# Revit family: КПД_Eng
name_source: partatom
category: Duct Accessories
units: mm (PartAtom-declared; Revit-internal decimal feet)

## family parameters
Always vertical = Yes
Cut with Voids When Loaded = No
Part Type = Attaches To
Round Connector Dimension = Use Diameter
Shared = No
Work Plane-Based = No

## types (184) — shared parameters
00_20_Manufacturer = Vents
00_20_Name = Multi-purpose fire safety smoke damper
Frequency = 50 Hz
Load Classification = HVAC
Maintenance zone material = <By Category>
Manufacturer = Vents
Maximum Air Flow = 0.0 L/s
Number of Fase = 1
URL = https://ventilation-system.com
Width = 160 mm  [stored 0.524934 ft]
zero-valued in all types: Default Elevation

## per-type parameters (varying)
| type | 00_20_Type | Actuator location (inside) | Actuator location (outside) | Apparent Load | B | B1 | B2 | B3 | Bn | Casing Material | H | H1 | H2 | H3 | Height | Hn | Length | Number of sashes | Two flanges | Voltage | Weight |
| KPD-300х300-2-PV24-SN | KPD-300х300-2-PV24-SN | No | Yes | 9 VA | 300 mm | 330 mm | 360 mm  [stored 1.1811 ft] | 165 mm  [stored 0.541339 ft] | 310 mm  [stored 1.01706 ft] | Steel, galvanized | 300 mm | 330 mm | 360 mm  [stored 1.1811 ft] | 50 mm  [stored 0.164042 ft] | 360 mm  [stored 1.1811 ft] | 310 mm  [stored 1.01706 ft] | 360 mm  [stored 1.1811 ft] | 1 | Yes | 24 V | 6.30 kg |
| KPD-1400х1400-2-PV24-SN | KPD-1400х1400-2-PV24-SN | No | Yes | 18 VA | 1400 mm | 1430 mm | 1460 mm | 715 mm | 1410 mm | Steel, galvanized | 1400 mm | 1430 mm | 1460 mm | 600 mm | 1460 mm | 1410 mm | 1460 mm | 4 | Yes | 24 V | 48.00 kg |
| KPD-300х300-1-PV24-SN | KPD-300х300-1-PV24-SN | No | Yes | 9 VA | 300 mm | 330 mm | 360 mm  [stored 1.1811 ft] | 165 mm  [stored 0.541339 ft] | 310 mm  [stored 1.01706 ft] | Steel, galvanized | 300 mm | 330 mm | 360 mm  [stored 1.1811 ft] | 50 mm  [stored 0.164042 ft] | 360 mm  [stored 1.1811 ft] | 310 mm  [stored 1.01706 ft] | 360 mm  [stored 1.1811 ft] | 1 | No | 24 V | 6.30 kg |
| KPD-1400х1400-1-PV24-SN | KPD-1400х1400-1-PV24-SN | No | Yes | 18 VA | 1400 mm | 1430 mm | 1460 mm | 715 mm | 1410 mm | Steel, galvanized | 1400 mm | 1430 mm | 1460 mm | 600 mm | 1460 mm | 1410 mm | 1460 mm | 4 | No | 24 V | 48.00 kg |
| KPD-300х300-1-PV24-VN | KPD-300х300-1-PV24-VN | Yes | No | 9 VA | 300 mm | 330 mm | 360 mm  [stored 1.1811 ft] | 165 mm  [stored 0.541339 ft] | 310 mm  [stored 1.01706 ft] | Steel, galvanized | 300 mm | 330 mm | 360 mm  [stored 1.1811 ft] | 50 mm  [stored 0.164042 ft] | 360 mm  [stored 1.1811 ft] | 310 mm  [stored 1.01706 ft] | 360 mm  [stored 1.1811 ft] | 1 | No | 24 V | 6.30 kg |
| KPD-300х300-2-PV24-VN | KPD-300х300-2-PV24-VN | Yes | No | 9 VA | 300 mm | 330 mm | 360 mm  [stored 1.1811 ft] | 165 mm  [stored 0.541339 ft] | 310 mm  [stored 1.01706 ft] | Cover Grid Cross | 300 mm | 330 mm | 360 mm  [stored 1.1811 ft] | 50 mm  [stored 0.164042 ft] | 360 mm  [stored 1.1811 ft] | 310 mm  [stored 1.01706 ft] | 360 mm  [stored 1.1811 ft] | 1 | Yes | 24 V | 6.30 kg |
| KPD-1400х1400-1-PV24-VN | KPD-1400х1400-1-PV24-VN | Yes | No | 18 VA | 1400 mm | 1430 mm | 1460 mm | 715 mm | 1410 mm | Steel, galvanized | 1400 mm | 1430 mm | 1460 mm | 600 mm | 1460 mm | 1410 mm | 1460 mm | 4 | No | 24 V | 48.00 kg |
| KPD-1400х1400-2-PV24-VN | KPD-1400х1400-2-PV24-VN | Yes | No | 18 VA | 1400 mm | 1430 mm | 1460 mm | 715 mm | 1410 mm | Steel, galvanized | 1400 mm | 1430 mm | 1460 mm | 600 mm | 1460 mm | 1410 mm | 1460 mm | 4 | Yes | 24 V | 48.00 kg |
| KPD-300х300-1-PV230-VN | KPD-300х300-1-PV230-VN | Yes | No | 12 VA | 300 mm | 330 mm | 360 mm  [stored 1.1811 ft] | 165 mm  [stored 0.541339 ft] | 310 mm  [stored 1.01706 ft] | Steel, galvanized | 300 mm | 330 mm | 360 mm  [stored 1.1811 ft] | 50 mm  [stored 0.164042 ft] | 360 mm  [stored 1.1811 ft] | 310 mm  [stored 1.01706 ft] | 360 mm  [stored 1.1811 ft] | 1 | No | 230 V | 6.30 kg |
| KPD-300х300-1-PV230-SN | KPD-300х300-1-PV230-SN | No | Yes | 12 VA | 300 mm | 330 mm | 360 mm  [stored 1.1811 ft] | 165 mm  [stored 0.541339 ft] | 310 mm  [stored 1.01706 ft] | Steel, galvanized | 300 mm | 330 mm | 360 mm  [stored 1.1811 ft] | 50 mm  [stored 0.164042 ft] | 360 mm  [stored 1.1811 ft] | 310 mm  [stored 1.01706 ft] | 360 mm  [stored 1.1811 ft] | 1 | No | 230 V | 6.30 kg |
| KPD-300х300-2-PV230-VN | KPD-300х300-2-PV230-VN | Yes | No | 12 VA | 300 mm | 330 mm | 360 mm  [stored 1.1811 ft] | 165 mm  [stored 0.541339 ft] | 310 mm  [stored 1.01706 ft] | Steel, galvanized | 300 mm | 330 mm | 360 mm  [stored 1.1811 ft] | 50 mm  [stored 0.164042 ft] | 360 mm  [stored 1.1811 ft] | 310 mm  [stored 1.01706 ft] | 360 mm  [stored 1.1811 ft] | 1 | Yes | 230 V | 6.30 kg |
| KPD-300х300-2-PV230-SN | KPD-300х300-2-PV230-SN | No | Yes | 12 VA | 300 mm | 330 mm | 360 mm  [stored 1.1811 ft] | 165 mm  [stored 0.541339 ft] | 310 mm  [stored 1.01706 ft] | Steel, galvanized | 300 mm | 330 mm | 360 mm  [stored 1.1811 ft] | 50 mm  [stored 0.164042 ft] | 360 mm  [stored 1.1811 ft] | 310 mm  [stored 1.01706 ft] | 360 mm  [stored 1.1811 ft] | 1 | Yes | 230 V | 6.30 kg |
| KPD-1400х1400-1-PV230-VN | KPD-1400х1400-1-PV230-VN | Yes | No | 15 VA | 1400 mm | 1430 mm | 1460 mm | 715 mm | 1410 mm | Steel, galvanized | 1400 mm | 1430 mm | 1460 mm | 600 mm | 1460 mm | 1410 mm | 1460 mm | 4 | No | 230 V | 48.00 kg |
| KPD-1400х1400-1-PV230-SN | KPD-1400х1400-1-PV230-SN | No | Yes | 15 VA | 1400 mm | 1430 mm | 1460 mm | 715 mm | 1410 mm | Steel, galvanized | 1400 mm | 1430 mm | 1460 mm | 600 mm | 1460 mm | 1410 mm | 1460 mm | 4 | No | 230 V | 48.00 kg |
| KPD-1400х1400-2-PV230-VN | KPD-1400х1400-2-PV230-VN | Yes | No | 15 VA | 1400 mm | 1430 mm | 1460 mm | 715 mm | 1410 mm | Steel, galvanized | 1400 mm | 1430 mm | 1460 mm | 600 mm | 1460 mm | 1410 mm | 1460 mm | 4 | Yes | 230 V | 48.00 kg |
| KPD-1400х1400-2-PV230-SN | KPD-1400х1400-2-PV230-SN | No | Yes | 15 VA | 1400 mm | 1430 mm | 1460 mm | 715 mm | 1410 mm | Steel, galvanized | 1400 mm | 1430 mm | 1460 mm | 600 mm | 1460 mm | 1410 mm | 1460 mm | 4 | Yes | 230 V | 48.00 kg |
| KPD-350х350-1-PV230-VN | KPD-350х350-1-PV230-VN | Yes | No | 12 VA | 350 mm  [stored 1.14829 ft] | 380 mm | 410 mm  [stored 1.34514 ft] | 190 mm | 360 mm  [stored 1.1811 ft] | Steel, galvanized | 350 mm  [stored 1.14829 ft] | 380 mm | 410 mm  [stored 1.34514 ft] | 75 mm  [stored 0.246063 ft] | 410 mm  [stored 1.34514 ft] | 360 mm  [stored 1.1811 ft] | 410 mm  [stored 1.34514 ft] | 1 | No | 230 V | 7.30 kg |
| KPD-350х350-1-PV230-SN | KPD-350х350-1-PV230-SN | No | Yes | 12 VA | 350 mm  [stored 1.14829 ft] | 380 mm | 410 mm  [stored 1.34514 ft] | 190 mm | 360 mm  [stored 1.1811 ft] | Steel, galvanized | 350 mm  [stored 1.14829 ft] | 380 mm | 410 mm  [stored 1.34514 ft] | 75 mm  [stored 0.246063 ft] | 410 mm  [stored 1.34514 ft] | 360 mm  [stored 1.1811 ft] | 410 mm  [stored 1.34514 ft] | 1 | No | 230 V | 7.30 kg |
| KPD-350х350-1-PV24-VN | KPD-350х350-1-PV24-VN | Yes | No | 9 VA | 350 mm  [stored 1.14829 ft] | 380 mm | 410 mm  [stored 1.34514 ft] | 190 mm | 360 mm  [stored 1.1811 ft] | Steel, galvanized | 350 mm  [stored 1.14829 ft] | 380 mm | 410 mm  [stored 1.34514 ft] | 75 mm  [stored 0.246063 ft] | 410 mm  [stored 1.34514 ft] | 360 mm  [stored 1.1811 ft] | 410 mm  [stored 1.34514 ft] | 1 | No | 24 V | 7.30 kg |
| KPD-350х350-1-PV24-SN | KPD-350х350-1-PV24-SN | No | Yes | 9 VA | 350 mm  [stored 1.14829 ft] | 380 mm | 410 mm  [stored 1.34514 ft] | 190 mm | 360 mm  [stored 1.1811 ft] | Steel, galvanized | 350 mm  [stored 1.14829 ft] | 380 mm | 410 mm  [stored 1.34514 ft] | 75 mm  [stored 0.246063 ft] | 410 mm  [stored 1.34514 ft] | 360 mm  [stored 1.1811 ft] | 410 mm  [stored 1.34514 ft] | 1 | No | 24 V | 7.30 kg |
| KPD-350х350-2-PV230-VN | KPD-350х350-2-PV230-VN | Yes | No | 12 VA | 350 mm  [stored 1.14829 ft] | 380 mm | 410 mm  [stored 1.34514 ft] | 190 mm | 360 mm  [stored 1.1811 ft] | Steel, galvanized | 350 mm  [stored 1.14829 ft] | 380 mm | 410 mm  [stored 1.34514 ft] | 75 mm  [stored 0.246063 ft] | 410 mm  [stored 1.34514 ft] | 360 mm  [stored 1.1811 ft] | 410 mm  [stored 1.34514 ft] | 1 | Yes | 230 V | 7.30 kg |
| KPD-350х350-2-PV230-SN | KPD-350х350-2-PV230-SN | No | Yes | 12 VA | 350 mm  [stored 1.14829 ft] | 380 mm | 410 mm  [stored 1.34514 ft] | 190 mm | 360 mm  [stored 1.1811 ft] | Steel, galvanized | 350 mm  [stored 1.14829 ft] | 380 mm | 410 mm  [stored 1.34514 ft] | 75 mm  [stored 0.246063 ft] | 410 mm  [stored 1.34514 ft] | 360 mm  [stored 1.1811 ft] | 410 mm  [stored 1.34514 ft] | 1 | Yes | 230 V | 7.30 kg |
| KPD-350х350-2-PV24-VN | KPD-350х350-2-PV24-VN | Yes | No | 9 VA | 350 mm  [stored 1.14829 ft] | 380 mm | 410 mm  [stored 1.34514 ft] | 190 mm | 360 mm  [stored 1.1811 ft] | Steel, galvanized | 350 mm  [stored 1.14829 ft] | 380 mm | 410 mm  [stored 1.34514 ft] | 75 mm  [stored 0.246063 ft] | 410 mm  [stored 1.34514 ft] | 360 mm  [stored 1.1811 ft] | 410 mm  [stored 1.34514 ft] | 1 | Yes | 24 V | 7.30 kg |
| KPD-350х350-2-PV24-SN | KPD-350х350-2-PV24-SN | No | Yes | 9 VA | 350 mm  [stored 1.14829 ft] | 380 mm | 410 mm  [stored 1.34514 ft] | 190 mm | 360 mm  [stored 1.1811 ft] | Steel, galvanized | 350 mm  [stored 1.14829 ft] | 380 mm | 410 mm  [stored 1.34514 ft] | 75 mm  [stored 0.246063 ft] | 410 mm  [stored 1.34514 ft] | 360 mm  [stored 1.1811 ft] | 410 mm  [stored 1.34514 ft] | 1 | Yes | 24 V | 7.30 kg |
| KPD-400х400-1-PV230-VN | KPD-400х400-1-PV230-VN | Yes | No | 12 VA | 400 mm  [stored 1.31234 ft] | 430 mm  [stored 1.41076 ft] | 460 mm  [stored 1.50919 ft] | 215 mm  [stored 0.705381 ft] | 410 mm  [stored 1.34514 ft] | Steel, galvanized | 400 mm  [stored 1.31234 ft] | 430 mm  [stored 1.41076 ft] | 460 mm  [stored 1.50919 ft] | 100 mm  [stored 0.328084 ft] | 460 mm  [stored 1.50919 ft] | 410 mm  [stored 1.34514 ft] | 460 mm  [stored 1.50919 ft] | 1 | No | 230 V | 0.00 kg |
| KPD-400х400-1-PV230-SN | KPD-400х400-1-PV230-SN | No | Yes | 12 VA | 400 mm  [stored 1.31234 ft] | 430 mm  [stored 1.41076 ft] | 460 mm  [stored 1.50919 ft] | 215 mm  [stored 0.705381 ft] | 410 mm  [stored 1.34514 ft] | Steel, galvanized | 400 mm  [stored 1.31234 ft] | 430 mm  [stored 1.41076 ft] | 460 mm  [stored 1.50919 ft] | 100 mm  [stored 0.328084 ft] | 460 mm  [stored 1.50919 ft] | 410 mm  [stored 1.34514 ft] | 460 mm  [stored 1.50919 ft] | 1 | No | 230 V | 8.20 kg |
| KPD-400х400-1-PV24-SN | KPD-400х400-1-PV24-SN | No | Yes | 9 VA | 400 mm  [stored 1.31234 ft] | 430 mm  [stored 1.41076 ft] | 460 mm  [stored 1.50919 ft] | 215 mm  [stored 0.705381 ft] | 410 mm  [stored 1.34514 ft] | Steel, galvanized | 400 mm  [stored 1.31234 ft] | 430 mm  [stored 1.41076 ft] | 460 mm  [stored 1.50919 ft] | 100 mm  [stored 0.328084 ft] | 460 mm  [stored 1.50919 ft] | 410 mm  [stored 1.34514 ft] | 460 mm  [stored 1.50919 ft] | 1 | No | 24 V | 8.20 kg |
| KPD-400х400-1-PV24-VN | KPD-400х400-1-PV24-VN | Yes | No | 9 VA | 400 mm  [stored 1.31234 ft] | 430 mm  [stored 1.41076 ft] | 460 mm  [stored 1.50919 ft] | 215 mm  [stored 0.705381 ft] | 410 mm  [stored 1.34514 ft] | Steel, galvanized | 400 mm  [stored 1.31234 ft] | 430 mm  [stored 1.41076 ft] | 460 mm  [stored 1.50919 ft] | 100 mm  [stored 0.328084 ft] | 460 mm  [stored 1.50919 ft] | 410 mm  [stored 1.34514 ft] | 460 mm  [stored 1.50919 ft] | 1 | No | 24 V | 8.20 kg |
| KPD-400х400-2-PV230-VN | KPD-400х400-2-PV230-VN | Yes | No | 12 VA | 400 mm  [stored 1.31234 ft] | 430 mm  [stored 1.41076 ft] | 460 mm  [stored 1.50919 ft] | 215 mm  [stored 0.705381 ft] | 410 mm  [stored 1.34514 ft] | Steel, galvanized | 400 mm  [stored 1.31234 ft] | 430 mm  [stored 1.41076 ft] | 460 mm  [stored 1.50919 ft] | 100 mm  [stored 0.328084 ft] | 460 mm  [stored 1.50919 ft] | 410 mm  [stored 1.34514 ft] | 460 mm  [stored 1.50919 ft] | 1 | Yes | 230 V | 8.20 kg |
| KPD-400х400-2-PV230-SN | KPD-400х400-2-PV230-SN | No | Yes | 12 VA | 400 mm  [stored 1.31234 ft] | 430 mm  [stored 1.41076 ft] | 460 mm  [stored 1.50919 ft] | 215 mm  [stored 0.705381 ft] | 410 mm  [stored 1.34514 ft] | Steel, galvanized | 400 mm  [stored 1.31234 ft] | 430 mm  [stored 1.41076 ft] | 460 mm  [stored 1.50919 ft] | 100 mm  [stored 0.328084 ft] | 460 mm  [stored 1.50919 ft] | 410 mm  [stored 1.34514 ft] | 460 mm  [stored 1.50919 ft] | 1 | Yes | 230 V | 8.20 kg |
| KPD-400х400-2-PV24-VN | KPD-400х400-2-PV24-VN | Yes | No | 9 VA | 400 mm  [stored 1.31234 ft] | 430 mm  [stored 1.41076 ft] | 460 mm  [stored 1.50919 ft] | 215 mm  [stored 0.705381 ft] | 410 mm  [stored 1.34514 ft] | Steel, galvanized | 400 mm  [stored 1.31234 ft] | 430 mm  [stored 1.41076 ft] | 460 mm  [stored 1.50919 ft] | 100 mm  [stored 0.328084 ft] | 460 mm  [stored 1.50919 ft] | 410 mm  [stored 1.34514 ft] | 460 mm  [stored 1.50919 ft] | 1 | Yes | 24 V | 8.20 kg |
| KPD-400х400-2-PV24-SN | KPD-400х400-2-PV24-SN | No | Yes | 9 VA | 400 mm  [stored 1.31234 ft] | 430 mm  [stored 1.41076 ft] | 460 mm  [stored 1.50919 ft] | 215 mm  [stored 0.705381 ft] | 410 mm  [stored 1.34514 ft] | Steel, galvanized | 400 mm  [stored 1.31234 ft] | 430 mm  [stored 1.41076 ft] | 460 mm  [stored 1.50919 ft] | 100 mm  [stored 0.328084 ft] | 460 mm  [stored 1.50919 ft] | 410 mm  [stored 1.34514 ft] | 460 mm  [stored 1.50919 ft] | 1 | Yes | 24 V | 8.20 kg |
| KPD-450х450-1-PV230-VN | KPD-450х450-1-PV230-VN | Yes | No | 12 VA | 450 mm  [stored 1.47638 ft] | 480 mm | 510 mm | 240 mm  [stored 0.787402 ft] | 460 mm  [stored 1.50919 ft] | Steel, galvanized | 450 mm  [stored 1.47638 ft] | 480 mm | 510 mm | 125 mm  [stored 0.410105 ft] | 510 mm | 460 mm  [stored 1.50919 ft] | 510 mm | 1 | No | 230 V | 9.50 kg |
| KPD-450х450-1-PV230-SN | KPD-450х450-1-PV230-SN | No | Yes | 12 VA | 450 mm  [stored 1.47638 ft] | 480 mm | 510 mm | 240 mm  [stored 0.787402 ft] | 460 mm  [stored 1.50919 ft] | Steel, galvanized | 450 mm  [stored 1.47638 ft] | 480 mm | 510 mm | 125 mm  [stored 0.410105 ft] | 510 mm | 460 mm  [stored 1.50919 ft] | 510 mm | 1 | No | 230 V | 9.50 kg |
| KPD-450х450-1-PV24-VN | KPD-450х450-1-PV24-VN | Yes | No | 9 VA | 450 mm  [stored 1.47638 ft] | 480 mm | 510 mm | 240 mm  [stored 0.787402 ft] | 460 mm  [stored 1.50919 ft] | Steel, galvanized | 450 mm  [stored 1.47638 ft] | 480 mm | 510 mm | 125 mm  [stored 0.410105 ft] | 510 mm | 460 mm  [stored 1.50919 ft] | 510 mm | 1 | No | 24 V | 9.50 kg |
| KPD-450х450-1-PV24-SN | KPD-450х450-1-PV24-SN | No | Yes | 9 VA | 450 mm  [stored 1.47638 ft] | 480 mm | 510 mm | 240 mm  [stored 0.787402 ft] | 460 mm  [stored 1.50919 ft] | Steel, galvanized | 450 mm  [stored 1.47638 ft] | 480 mm | 510 mm | 125 mm  [stored 0.410105 ft] | 510 mm | 460 mm  [stored 1.50919 ft] | 510 mm | 1 | No | 24 V | 9.50 kg |
| KPD-450х450-2-PV230-VN | KPD-450х450-2-PV230-VN | Yes | No | 12 VA | 450 mm  [stored 1.47638 ft] | 480 mm | 510 mm | 240 mm  [stored 0.787402 ft] | 460 mm  [stored 1.50919 ft] | Steel, galvanized | 450 mm  [stored 1.47638 ft] | 480 mm | 510 mm | 125 mm  [stored 0.410105 ft] | 510 mm | 460 mm  [stored 1.50919 ft] | 510 mm | 1 | Yes | 230 V | 9.50 kg |
| KPD-450х450-2-PV230-SN | KPD-450х450-2-PV230-SN | No | Yes | 12 VA | 450 mm  [stored 1.47638 ft] | 480 mm | 510 mm | 240 mm  [stored 0.787402 ft] | 460 mm  [stored 1.50919 ft] | Steel, galvanized | 450 mm  [stored 1.47638 ft] | 480 mm | 510 mm | 125 mm  [stored 0.410105 ft] | 510 mm | 460 mm  [stored 1.50919 ft] | 510 mm | 1 | Yes | 230 V | 9.50 kg |
| KPD-450х450-2-PV24-VN | KPD-450х450-2-PV24-VN | Yes | No | 9 VA | 450 mm  [stored 1.47638 ft] | 480 mm | 510 mm | 240 mm  [stored 0.787402 ft] | 460 mm  [stored 1.50919 ft] | Steel, galvanized | 450 mm  [stored 1.47638 ft] | 480 mm | 510 mm | 125 mm  [stored 0.410105 ft] | 510 mm | 460 mm  [stored 1.50919 ft] | 510 mm | 1 | Yes | 24 V | 9.50 kg |
| KPD-450х450-2-PV24-SN | KPD-450х450-2-PV24-SN | No | Yes | 9 VA | 450 mm  [stored 1.47638 ft] | 480 mm | 510 mm | 240 mm  [stored 0.787402 ft] | 460 mm  [stored 1.50919 ft] | Steel, galvanized | 450 mm  [stored 1.47638 ft] | 480 mm | 510 mm | 125 mm  [stored 0.410105 ft] | 510 mm | 460 mm  [stored 1.50919 ft] | 510 mm | 1 | Yes | 24 V | 9.50 kg |
| KPD-500х500-1-PV230-VN | KPD-500х500-1-PV230-VN | Yes | No | 12 VA | 500 mm | 530 mm | 560 mm | 265 mm  [stored 0.869423 ft] | 510 mm | Steel, galvanized | 500 mm | 530 mm | 560 mm | 150 mm | 560 mm | 510 mm | 560 mm | 1 | No | 230 V | 10.60 kg |
| KPD-500х500-1-PV230-SN | KPD-500х500-1-PV230-SN | No | Yes | 12 VA | 500 mm | 530 mm | 560 mm | 265 mm  [stored 0.869423 ft] | 510 mm | Steel, galvanized | 500 mm | 530 mm | 560 mm | 150 mm | 560 mm | 510 mm | 560 mm | 1 | No | 230 V | 10.60 kg |
| KPD-500х500-1-PV24-VN | KPD-500х500-1-PV24-VN | Yes | No | 9 VA | 500 mm | 530 mm | 560 mm | 265 mm  [stored 0.869423 ft] | 510 mm | Steel, galvanized | 500 mm | 530 mm | 560 mm | 150 mm | 560 mm | 510 mm | 560 mm | 1 | No | 24 V | 10.60 kg |
| KPD-500х500-1-PV24-SN | KPD-500х500-1-PV24-SN | No | Yes | 9 VA | 500 mm | 530 mm | 560 mm | 265 mm  [stored 0.869423 ft] | 510 mm | Steel, galvanized | 500 mm | 530 mm | 560 mm | 150 mm | 560 mm | 510 mm | 560 mm | 1 | No | 24 V | 10.60 kg |
| KPD-500х500-2-PV230-VN | KPD-500х500-2-PV230-VN | Yes | No | 12 VA | 500 mm | 530 mm | 560 mm | 265 mm  [stored 0.869423 ft] | 510 mm | Steel, galvanized | 500 mm | 530 mm | 560 mm | 150 mm | 560 mm | 510 mm | 560 mm | 1 | Yes | 230 V | 10.60 kg |
| KPD-500х500-2-PV230-SN | KPD-500х500-2-PV230-SN | No | Yes | 12 VA | 500 mm | 530 mm | 560 mm | 265 mm  [stored 0.869423 ft] | 510 mm | Steel, galvanized | 500 mm | 530 mm | 560 mm | 150 mm | 560 mm | 510 mm | 560 mm | 1 | Yes | 230 V | 10.60 kg |
| KPD-500х500-2-PV24-VN | KPD-500х500-2-PV24-VN | Yes | No | 9 VA | 500 mm | 530 mm | 560 mm | 265 mm  [stored 0.869423 ft] | 510 mm | Steel, galvanized | 500 mm | 530 mm | 560 mm | 150 mm | 560 mm | 510 mm | 560 mm | 1 | Yes | 24 V | 10.60 kg |
| KPD-500х500-2-PV24-SN | KPD-500х500-2-PV24-SN | No | Yes | 9 VA | 500 mm | 530 mm | 560 mm | 265 mm  [stored 0.869423 ft] | 510 mm | Steel, galvanized | 500 mm | 530 mm | 560 mm | 150 mm | 560 mm | 510 mm | 560 mm | 1 | Yes | 24 V | 10.60 kg |
| KPD-550х550-1-PV230-VN | KPD-550х550-1-PV230-VN | Yes | No | 15 VA | 550 mm | 580 mm | 610 mm | 290 mm  [stored 0.951444 ft] | 560 mm | Steel, galvanized | 550 mm | 580 mm | 610 mm | 175 mm  [stored 0.574147 ft] | 610 mm | 560 mm | 610 mm | 1 | No | 230 V | 11.90 kg |
| KPD-550х550-1-PV230-SN | KPD-550х550-1-PV230-SN | No | Yes | 15 VA | 550 mm | 580 mm | 610 mm | 290 mm  [stored 0.951444 ft] | 560 mm | Steel, galvanized | 550 mm | 580 mm | 610 mm | 175 mm  [stored 0.574147 ft] | 610 mm | 560 mm | 610 mm | 1 | No | 230 V | 11.90 kg |
| KPD-550х550-1-PV24-VN | KPD-550х550-1-PV24-VN | Yes | No | 18 VA | 550 mm | 580 mm | 610 mm | 290 mm  [stored 0.951444 ft] | 560 mm | Steel, galvanized | 550 mm | 580 mm | 610 mm | 175 mm  [stored 0.574147 ft] | 610 mm | 560 mm | 610 mm | 1 | No | 24 V | 11.90 kg |
| KPD-550х550-1-PV24-SN | KPD-550х550-1-PV24-SN | No | Yes | 18 VA | 550 mm | 580 mm | 610 mm | 290 mm  [stored 0.951444 ft] | 560 mm | Steel, galvanized | 550 mm | 580 mm | 610 mm | 175 mm  [stored 0.574147 ft] | 610 mm | 560 mm | 610 mm | 1 | No | 24 V | 11.90 kg |
| KPD-550х550-2-PV230-VN | KPD-550х550-2-PV230-VN | Yes | No | 15 VA | 550 mm | 580 mm | 610 mm | 290 mm  [stored 0.951444 ft] | 560 mm | Steel, galvanized | 550 mm | 580 mm | 610 mm | 175 mm  [stored 0.574147 ft] | 610 mm | 560 mm | 610 mm | 1 | Yes | 230 V | 11.90 kg |
| KPD-550х550-2-PV230-SN | KPD-550х550-2-PV230-SN | No | Yes | 15 VA | 550 mm | 580 mm | 610 mm | 290 mm  [stored 0.951444 ft] | 560 mm | Steel, galvanized | 550 mm | 580 mm | 610 mm | 175 mm  [stored 0.574147 ft] | 610 mm | 560 mm | 610 mm | 1 | Yes | 230 V | 11.90 kg |
| KPD-550х550-2-PV24-VN | KPD-550х550-2-PV24-VN | Yes | No | 18 VA | 550 mm | 580 mm | 610 mm | 290 mm  [stored 0.951444 ft] | 560 mm | Steel, galvanized | 550 mm | 580 mm | 610 mm | 175 mm  [stored 0.574147 ft] | 610 mm | 560 mm | 610 mm | 1 | Yes | 24 V | 11.90 kg |
| KPD-550х550-2-PV24-SN | KPD-550х550-2-PV24-SN | No | Yes | 18 VA | 550 mm | 580 mm | 610 mm | 290 mm  [stored 0.951444 ft] | 560 mm | Steel, galvanized | 550 mm | 580 mm | 610 mm | 175 mm  [stored 0.574147 ft] | 610 mm | 560 mm | 610 mm | 1 | Yes | 24 V | 11.90 kg |
| KPD-600х600-1-PV230-VN | KPD-600х600-1-PV230-VN | Yes | No | 15 VA | 600 mm | 630 mm | 660 mm | 315 mm  [stored 1.03346 ft] | 610 mm | Steel, galvanized | 600 mm | 630 mm | 660 mm | 200 mm  [stored 0.656168 ft] | 660 mm | 610 mm | 660 mm | 1 | No | 230 V | 13.20 kg |
| KPD-600х600-1-PV230-SN | KPD-600х600-1-PV230-SN | No | Yes | 15 VA | 600 mm | 630 mm | 660 mm | 315 mm  [stored 1.03346 ft] | 610 mm | Steel, galvanized | 600 mm | 630 mm | 660 mm | 200 mm  [stored 0.656168 ft] | 660 mm | 610 mm | 660 mm | 1 | No | 230 V | 13.20 kg |
| KPD-600х600-1-PV24-VN | KPD-600х600-1-PV24-VN | Yes | No | 18 VA | 600 mm | 630 mm | 660 mm | 315 mm  [stored 1.03346 ft] | 610 mm | Steel, galvanized | 600 mm | 630 mm | 660 mm | 200 mm  [stored 0.656168 ft] | 660 mm | 610 mm | 660 mm | 1 | No | 24 V | 13.20 kg |
| KPD-600х600-1-PV24-SN | KPD-600х600-1-PV24-SN | No | Yes | 18 VA | 600 mm | 630 mm | 660 mm | 315 mm  [stored 1.03346 ft] | 610 mm | Steel, galvanized | 600 mm | 630 mm | 660 mm | 200 mm  [stored 0.656168 ft] | 660 mm | 610 mm | 660 mm | 1 | No | 24 V | 13.20 kg |
| KPD-600х600-2-PV230-VN | KPD-600х600-2-PV230-VN | Yes | No | 15 VA | 600 mm | 630 mm | 660 mm | 315 mm  [stored 1.03346 ft] | 610 mm | Steel, galvanized | 600 mm | 630 mm | 660 mm | 200 mm  [stored 0.656168 ft] | 660 mm | 610 mm | 660 mm | 1 | Yes | 230 V | 13.20 kg |
| KPD-600х600-2-PV230-SN | KPD-600х600-2-PV230-SN | No | Yes | 15 VA | 600 mm | 630 mm | 660 mm | 315 mm  [stored 1.03346 ft] | 610 mm | Steel, galvanized | 600 mm | 630 mm | 660 mm | 200 mm  [stored 0.656168 ft] | 660 mm | 610 mm | 660 mm | 1 | Yes | 230 V | 13.20 kg |
| KPD-600х600-2-PV24-VN | KPD-600х600-2-PV24-VN | Yes | No | 18 VA | 600 mm | 630 mm | 660 mm | 315 mm  [stored 1.03346 ft] | 610 mm | Steel, galvanized | 600 mm | 630 mm | 660 mm | 200 mm  [stored 0.656168 ft] | 660 mm | 610 mm | 660 mm | 1 | Yes | 24 V | 13.20 kg |
| KPD-600х600-2-PV24-SN | KPD-600х600-2-PV24-SN | No | Yes | 18 VA | 600 mm | 630 mm | 660 mm | 315 mm  [stored 1.03346 ft] | 610 mm | Steel, galvanized | 600 mm | 630 mm | 660 mm | 200 mm  [stored 0.656168 ft] | 660 mm | 610 mm | 660 mm | 1 | Yes | 24 V | 13.20 kg |
| KPD-650х650-1-PV230-VN | KPD-650х650-1-PV230-VN | Yes | No | 15 VA | 650 mm | 680 mm | 710 mm | 340 mm  [stored 1.11549 ft] | 660 mm | Steel, galvanized | 650 mm | 680 mm | 710 mm | 225 mm  [stored 0.738189 ft] | 710 mm | 660 mm | 710 mm | 1 | No | 230 V | 14.50 kg |
| KPD-650х650-1-PV230-SN | KPD-650х650-1-PV230-SN | No | Yes | 15 VA | 650 mm | 680 mm | 710 mm | 340 mm  [stored 1.11549 ft] | 660 mm | Steel, galvanized | 650 mm | 680 mm | 710 mm | 225 mm  [stored 0.738189 ft] | 710 mm | 660 mm | 710 mm | 1 | No | 230 V | 14.50 kg |
| KPD-650х650-1-PV24-VN | KPD-650х650-1-PV24-VN | Yes | No | 18 VA | 650 mm | 680 mm | 710 mm | 340 mm  [stored 1.11549 ft] | 660 mm | Steel, galvanized | 650 mm | 680 mm | 710 mm | 225 mm  [stored 0.738189 ft] | 710 mm | 660 mm | 710 mm | 1 | No | 24 V | 14.50 kg |
| KPD-650х650-1-PV24-SN | KPD-650х650-1-PV24-SN | No | Yes | 18 VA | 650 mm | 680 mm | 710 mm | 340 mm  [stored 1.11549 ft] | 660 mm | Steel, galvanized | 650 mm | 680 mm | 710 mm | 225 mm  [stored 0.738189 ft] | 710 mm | 660 mm | 710 mm | 1 | No | 24 V | 14.50 kg |
| KPD-650х650-2-PV230-VN | KPD-650х650-2-PV230-VN | Yes | No | 15 VA | 650 mm | 680 mm | 710 mm | 340 mm  [stored 1.11549 ft] | 660 mm | Steel, galvanized | 650 mm | 680 mm | 710 mm | 225 mm  [stored 0.738189 ft] | 710 mm | 660 mm | 710 mm | 1 | Yes | 230 V | 14.50 kg |
| KPD-650х650-2-PV230-SN | KPD-650х650-2-PV230-SN | No | Yes | 15 VA | 650 mm | 680 mm | 710 mm | 340 mm  [stored 1.11549 ft] | 660 mm | Steel, galvanized | 650 mm | 680 mm | 710 mm | 225 mm  [stored 0.738189 ft] | 710 mm | 660 mm | 710 mm | 1 | Yes | 230 V | 14.50 kg |
| KPD-650х650-2-PV24-VN | KPD-650х650-2-PV24-VN | Yes | No | 18 VA | 650 mm | 680 mm | 710 mm | 340 mm  [stored 1.11549 ft] | 660 mm | Steel, galvanized | 650 mm | 680 mm | 710 mm | 225 mm  [stored 0.738189 ft] | 710 mm | 660 mm | 710 mm | 1 | Yes | 24 V | 14.50 kg |
| KPD-650х650-2-PV24-SN | KPD-650х650-2-PV24-SN | No | Yes | 18 VA | 650 mm | 680 mm | 710 mm | 340 mm  [stored 1.11549 ft] | 660 mm | Steel, galvanized | 650 mm | 680 mm | 710 mm | 225 mm  [stored 0.738189 ft] | 710 mm | 660 mm | 710 mm | 1 | Yes | 24 V | 14.50 kg |
| KPD-700х700-1-PV230-VN | KPD-700х700-1-PV230-VN | Yes | No | 15 VA | 700 mm | 730 mm | 760 mm | 365 mm  [stored 1.19751 ft] | 710 mm | Steel, galvanized | 700 mm | 730 mm | 760 mm | 250 mm  [stored 0.82021 ft] | 760 mm | 710 mm | 760 mm | 1 | No | 230 V | 16.00 kg |
| KPD-700х700-1-PV230-SN | KPD-700х700-1-PV230-SN | No | Yes | 15 VA | 700 mm | 730 mm | 760 mm | 365 mm  [stored 1.19751 ft] | 710 mm | Steel, galvanized | 700 mm | 730 mm | 760 mm | 250 mm  [stored 0.82021 ft] | 760 mm | 710 mm | 760 mm | 1 | No | 230 V | 16.00 kg |
| KPD-700х700-1-PV24-VN | KPD-700х700-1-PV24-VN | Yes | No | 18 VA | 700 mm | 730 mm | 760 mm | 365 mm  [stored 1.19751 ft] | 710 mm | Steel, galvanized | 700 mm | 730 mm | 760 mm | 250 mm  [stored 0.82021 ft] | 760 mm | 710 mm | 760 mm | 1 | No | 24 V | 16.00 kg |
| KPD-700х700-1-PV24-SN | KPD-700х700-1-PV24-SN | No | Yes | 18 VA | 700 mm | 730 mm | 760 mm | 365 mm  [stored 1.19751 ft] | 710 mm | Steel, galvanized | 700 mm | 730 mm | 760 mm | 250 mm  [stored 0.82021 ft] | 760 mm | 710 mm | 760 mm | 1 | No | 24 V | 16.00 kg |
| KPD-700х700-2-PV230-VN | KPD-700х700-2-PV230-VN | Yes | No | 15 VA | 700 mm | 730 mm | 760 mm | 365 mm  [stored 1.19751 ft] | 710 mm | Steel, galvanized | 700 mm | 730 mm | 760 mm | 250 mm  [stored 0.82021 ft] | 760 mm | 710 mm | 760 mm | 1 | Yes | 230 V | 16.00 kg |
| KPD-700х700-2-PV230-SN | KPD-700х700-2-PV230-SN | No | Yes | 15 VA | 700 mm | 730 mm | 760 mm | 365 mm  [stored 1.19751 ft] | 710 mm | Steel, galvanized | 700 mm | 730 mm | 760 mm | 250 mm  [stored 0.82021 ft] | 760 mm | 710 mm | 760 mm | 1 | Yes | 230 V | 16.00 kg |
| KPD-700х700-2-PV24-VN | KPD-700х700-2-PV24-VN | Yes | No | 18 VA | 700 mm | 730 mm | 760 mm | 365 mm  [stored 1.19751 ft] | 710 mm | Steel, galvanized | 700 mm | 730 mm | 760 mm | 250 mm  [stored 0.82021 ft] | 760 mm | 710 mm | 760 mm | 1 | Yes | 24 V | 16.00 kg |
| KPD-700х700-2-PV24-SN | KPD-700х700-2-PV24-SN | No | Yes | 18 VA | 700 mm | 730 mm | 760 mm | 365 mm  [stored 1.19751 ft] | 710 mm | Steel, galvanized | 700 mm | 730 mm | 760 mm | 250 mm  [stored 0.82021 ft] | 760 mm | 710 mm | 760 mm | 1 | Yes | 24 V | 16.00 kg |
| KPD-750х750-1-PV230-VN | KPD-750х750-1-PV230-VN | Yes | No | 15 VA | 750 mm | 780 mm | 810 mm | 390 mm  [stored 1.27953 ft] | 760 mm | Steel, galvanized | 750 mm | 780 mm | 810 mm | 275 mm | 810 mm | 760 mm | 810 mm | 1 | No | 230 V | 17.40 kg |
| KPD-750х750-1-PV230-SN | KPD-750х750-1-PV230-SN | No | Yes | 15 VA | 750 mm | 780 mm | 810 mm | 390 mm  [stored 1.27953 ft] | 760 mm | Steel, galvanized | 750 mm | 780 mm | 810 mm | 275 mm | 810 mm | 760 mm | 810 mm | 1 | No | 230 V | 17.40 kg |
| KPD-750х750-1-PV24-VN | KPD-750х750-1-PV24-VN | Yes | No | 18 VA | 750 mm | 780 mm | 810 mm | 390 mm  [stored 1.27953 ft] | 760 mm | Steel, galvanized | 750 mm | 780 mm | 810 mm | 275 mm | 810 mm | 760 mm | 810 mm | 1 | No | 24 V | 17.40 kg |
| KPD-750х750-1-PV24-SN | KPD-750х750-1-PV24-SN | No | Yes | 18 VA | 750 mm | 780 mm | 810 mm | 390 mm  [stored 1.27953 ft] | 760 mm | Steel, galvanized | 750 mm | 780 mm | 810 mm | 275 mm | 810 mm | 760 mm | 810 mm | 1 | No | 24 V | 17.40 kg |
| KPD-750х750-2-PV230-VN | KPD-750х750-2-PV230-VN | Yes | No | 15 VA | 750 mm | 780 mm | 810 mm | 390 mm  [stored 1.27953 ft] | 760 mm | Steel, galvanized | 750 mm | 780 mm | 810 mm | 275 mm | 810 mm | 760 mm | 810 mm | 1 | Yes | 230 V | 17.40 kg |
| KPD-750х750-2-PV230-SN | KPD-750х750-2-PV230-SN | No | Yes | 15 VA | 750 mm | 780 mm | 810 mm | 390 mm  [stored 1.27953 ft] | 760 mm | Steel, galvanized | 750 mm | 780 mm | 810 mm | 275 mm | 810 mm | 760 mm | 810 mm | 1 | Yes | 230 V | 17.40 kg |
| KPD-750х750-2-PV24-VN | KPD-750х750-2-PV24-VN | Yes | No | 18 VA | 750 mm | 780 mm | 810 mm | 390 mm  [stored 1.27953 ft] | 760 mm | Steel, galvanized | 750 mm | 780 mm | 810 mm | 275 mm | 810 mm | 760 mm | 810 mm | 1 | Yes | 24 V | 17.40 kg |
| KPD-750х750-2-PV24-SN | KPD-750х750-2-PV24-SN | No | Yes | 18 VA | 750 mm | 780 mm | 810 mm | 390 mm  [stored 1.27953 ft] | 760 mm | Steel, galvanized | 750 mm | 780 mm | 810 mm | 275 mm | 810 mm | 760 mm | 810 mm | 1 | Yes | 24 V | 17.40 kg |
| KPD-800х800-1-PV230-VN | KPD-800х800-1-PV230-VN | Yes | No | 15 VA | 800 mm | 830 mm | 860 mm | 415 mm  [stored 1.36155 ft] | 810 mm | Steel, galvanized | 800 mm | 830 mm | 860 mm | 300 mm | 860 mm | 810 mm | 860 mm | 1 | No | 230 V | 19.00 kg |
| KPD-800х800-1-PV230-SN | KPD-800х800-1-PV230-SN | No | Yes | 15 VA | 800 mm | 830 mm | 860 mm | 415 mm  [stored 1.36155 ft] | 810 mm | Steel, galvanized | 800 mm | 830 mm | 860 mm | 300 mm | 860 mm | 810 mm | 860 mm | 1 | No | 230 V | 19.00 kg |
| KPD-800х800-1-PV24-VN | KPD-800х800-1-PV24-VN | Yes | No | 18 VA | 800 mm | 830 mm | 860 mm | 415 mm  [stored 1.36155 ft] | 810 mm | Steel, galvanized | 800 mm | 830 mm | 860 mm | 300 mm | 860 mm | 810 mm | 860 mm | 1 | No | 24 V | 19.00 kg |
| KPD-800х800-1-PV24-SN | KPD-800х800-1-PV24-SN | No | Yes | 18 VA | 800 mm | 830 mm | 860 mm | 415 mm  [stored 1.36155 ft] | 810 mm | Steel, galvanized | 800 mm | 830 mm | 860 mm | 300 mm | 860 mm | 810 mm | 860 mm | 1 | No | 24 V | 19.00 kg |
| KPD-800х800-2-PV230-VN | KPD-800х800-2-PV230-VN | Yes | No | 15 VA | 800 mm | 830 mm | 860 mm | 415 mm  [stored 1.36155 ft] | 810 mm | Steel, galvanized | 800 mm | 830 mm | 860 mm | 300 mm | 860 mm | 810 mm | 860 mm | 1 | Yes | 230 V | 19.00 kg |
| KPD-800х800-2-PV230-SN | KPD-800х800-2-PV230-SN | No | Yes | 15 VA | 800 mm | 830 mm | 860 mm | 415 mm  [stored 1.36155 ft] | 810 mm | Steel, galvanized | 800 mm | 830 mm | 860 mm | 300 mm | 860 mm | 810 mm | 860 mm | 1 | Yes | 230 V | 19.00 kg |
| KPD-800х800-2-PV24-VN | KPD-800х800-2-PV24-VN | Yes | No | 18 VA | 800 mm | 830 mm | 860 mm | 415 mm  [stored 1.36155 ft] | 810 mm | Steel, galvanized | 800 mm | 830 mm | 860 mm | 300 mm | 860 mm | 810 mm | 860 mm | 1 | Yes | 24 V | 19.00 kg |
| KPD-800х800-2-PV24-SN | KPD-800х800-2-PV24-SN | No | Yes | 18 VA | 800 mm | 830 mm | 860 mm | 415 mm  [stored 1.36155 ft] | 810 mm | Steel, galvanized | 800 mm | 830 mm | 860 mm | 300 mm | 860 mm | 810 mm | 860 mm | 1 | Yes | 24 V | 19.00 kg |
| KPD-850х850-1-PV230-VN | KPD-850х850-1-PV230-VN | Yes | No | 15 VA | 850 mm | 880 mm | 910 mm | 440 mm  [stored 1.44357 ft] | 860 mm | Steel, galvanized | 850 mm | 880 mm | 910 mm | 325 mm  [stored 1.06627 ft] | 910 mm | 860 mm | 910 mm | 1 | No | 230 V | 20.60 kg |
| KPD-850х850-1-PV230-SN | KPD-850х850-1-PV230-SN | No | Yes | 15 VA | 850 mm | 880 mm | 910 mm | 440 mm  [stored 1.44357 ft] | 860 mm | Steel, galvanized | 850 mm | 880 mm | 910 mm | 325 mm  [stored 1.06627 ft] | 910 mm | 860 mm | 910 mm | 1 | No | 230 V | 20.60 kg |
| KPD-850х850-1-PV24-VN | KPD-850х850-1-PV24-VN | Yes | No | 18 VA | 850 mm | 880 mm | 910 mm | 440 mm  [stored 1.44357 ft] | 860 mm | Steel, galvanized | 850 mm | 880 mm | 910 mm | 325 mm  [stored 1.06627 ft] | 910 mm | 860 mm | 910 mm | 1 | No | 24 V | 20.60 kg |
| KPD-850х850-1-PV24-SN | KPD-850х850-1-PV24-SN | No | Yes | 18 VA | 850 mm | 880 mm | 910 mm | 440 mm  [stored 1.44357 ft] | 860 mm | Steel, galvanized | 850 mm | 880 mm | 910 mm | 325 mm  [stored 1.06627 ft] | 910 mm | 860 mm | 910 mm | 1 | No | 24 V | 20.60 kg |
| KPD-850х850-2-PV230-VN | KPD-850х850-2-PV230-VN | Yes | No | 15 VA | 850 mm | 880 mm | 910 mm | 440 mm  [stored 1.44357 ft] | 860 mm | Steel, galvanized | 850 mm | 880 mm | 910 mm | 325 mm  [stored 1.06627 ft] | 910 mm | 860 mm | 910 mm | 1 | Yes | 230 V | 20.60 kg |
| KPD-850х850-2-PV230-SN | KPD-850х850-2-PV230-SN | No | Yes | 15 VA | 850 mm | 880 mm | 910 mm | 440 mm  [stored 1.44357 ft] | 860 mm | Steel, galvanized | 850 mm | 880 mm | 910 mm | 325 mm  [stored 1.06627 ft] | 910 mm | 860 mm | 910 mm | 1 | Yes | 230 V | 20.60 kg |
| KPD-850х850-2-PV24-VN | KPD-850х850-2-PV24-VN | Yes | No | 18 VA | 850 mm | 880 mm | 910 mm | 440 mm  [stored 1.44357 ft] | 860 mm | Steel, galvanized | 850 mm | 880 mm | 910 mm | 325 mm  [stored 1.06627 ft] | 910 mm | 860 mm | 910 mm | 1 | Yes | 24 V | 20.60 kg |
| KPD-850х850-2-PV24-SN | KPD-850х850-2-PV24-SN | No | Yes | 18 VA | 850 mm | 880 mm | 910 mm | 440 mm  [stored 1.44357 ft] | 860 mm | Steel, galvanized | 850 mm | 880 mm | 910 mm | 325 mm  [stored 1.06627 ft] | 910 mm | 860 mm | 910 mm | 1 | Yes | 24 V | 20.60 kg |
| KPD-900х900-1-PV230-VN | KPD-900х900-1-PV230-VN | Yes | No | 15 VA | 900 mm | 930 mm | 960 mm | 465 mm  [stored 1.52559 ft] | 910 mm | Steel, galvanized | 900 mm | 930 mm | 960 mm | 350 mm  [stored 1.14829 ft] | 960 mm | 910 mm | 960 mm | 1 | No | 230 V | 19.00 kg |
| KPD-900х900-1-PV230-SN | KPD-900х900-1-PV230-SN | No | Yes | 15 VA | 900 mm | 930 mm | 960 mm | 465 mm  [stored 1.52559 ft] | 910 mm | Steel, galvanized | 900 mm | 930 mm | 960 mm | 350 mm  [stored 1.14829 ft] | 960 mm | 910 mm | 960 mm | 1 | No | 230 V | 19.00 kg |
| KPD-900х900-1-PV24-VN | KPD-900х900-1-PV24-VN | Yes | No | 18 VA | 900 mm | 930 mm | 960 mm | 465 mm  [stored 1.52559 ft] | 910 mm | Steel, galvanized | 900 mm | 930 mm | 960 mm | 350 mm  [stored 1.14829 ft] | 960 mm | 910 mm | 960 mm | 1 | No | 24 V | 19.00 kg |
| KPD-900х900-1-PV24-SN | KPD-900х900-1-PV24-SN | No | Yes | 18 VA | 900 mm | 930 mm | 960 mm | 465 mm  [stored 1.52559 ft] | 910 mm | Steel, galvanized | 900 mm | 930 mm | 960 mm | 350 mm  [stored 1.14829 ft] | 960 mm | 910 mm | 960 mm | 1 | No | 24 V | 19.00 kg |
| KPD-900х900-2-PV230-VN | KPD-900х900-2-PV230-VN | Yes | No | 15 VA | 900 mm | 930 mm | 960 mm | 465 mm  [stored 1.52559 ft] | 910 mm | Steel, galvanized | 900 mm | 930 mm | 960 mm | 350 mm  [stored 1.14829 ft] | 960 mm | 910 mm | 960 mm | 1 | Yes | 230 V | 19.00 kg |
| KPD-900х900-2-PV230-SN | KPD-900х900-2-PV230-SN | No | Yes | 15 VA | 900 mm | 930 mm | 960 mm | 465 mm  [stored 1.52559 ft] | 910 mm | Steel, galvanized | 900 mm | 930 mm | 960 mm | 350 mm  [stored 1.14829 ft] | 960 mm | 910 mm | 960 mm | 1 | Yes | 230 V | 19.00 kg |
| KPD-900х900-2-PV24-VN | KPD-900х900-2-PV24-VN | Yes | No | 18 VA | 900 mm | 930 mm | 960 mm | 465 mm  [stored 1.52559 ft] | 910 mm | Steel, galvanized | 900 mm | 930 mm | 960 mm | 350 mm  [stored 1.14829 ft] | 960 mm | 910 mm | 960 mm | 1 | Yes | 24 V | 19.00 kg |
| KPD-900х900-2-PV24-SN | KPD-900х900-2-PV24-SN | No | Yes | 18 VA | 900 mm | 930 mm | 960 mm | 465 mm  [stored 1.52559 ft] | 910 mm | Steel, galvanized | 900 mm | 930 mm | 960 mm | 350 mm  [stored 1.14829 ft] | 960 mm | 910 mm | 960 mm | 1 | Yes | 24 V | 19.00 kg |
| KPD-950х950-1-PV230-VN | KPD-950х950-1-PV230-VN | Yes | No | 15 VA | 950 mm | 980 mm | 1010 mm | 490 mm | 960 mm | Steel, galvanized | 950 mm | 980 mm | 1010 mm | 375 mm  [stored 1.23031 ft] | 1010 mm | 960 mm | 1010 mm | 1 | No | 230 V | 23.90 kg |
| KPD-950х950-1-PV230-SN | KPD-950х950-1-PV230-SN | No | Yes | 15 VA | 950 mm | 980 mm | 1010 mm | 490 mm | 960 mm | Steel, galvanized | 950 mm | 980 mm | 1010 mm | 375 mm  [stored 1.23031 ft] | 1010 mm | 960 mm | 1010 mm | 1 | No | 230 V | 23.90 kg |
| KPD-950х950-1-PV24-VN | KPD-950х950-1-PV24-VN | Yes | No | 18 VA | 950 mm | 980 mm | 1010 mm | 490 mm | 960 mm | Steel, galvanized | 950 mm | 980 mm | 1010 mm | 375 mm  [stored 1.23031 ft] | 1010 mm | 960 mm | 1010 mm | 1 | No | 24 V | 23.90 kg |
| KPD-950х950-1-PV24-SN | KPD-950х950-1-PV24-SN | No | Yes | 18 VA | 950 mm | 980 mm | 1010 mm | 490 mm | 960 mm | Steel, galvanized | 950 mm | 980 mm | 1010 mm | 375 mm  [stored 1.23031 ft] | 1010 mm | 960 mm | 1010 mm | 1 | No | 24 V | 23.90 kg |
| KPD-950х950-2-PV230-VN | KPD-950х950-2-PV230-VN | Yes | No | 15 VA | 950 mm | 980 mm | 1010 mm | 490 mm | 960 mm | Steel, galvanized | 950 mm | 980 mm | 1010 mm | 375 mm  [stored 1.23031 ft] | 1010 mm | 960 mm | 1010 mm | 1 | Yes | 230 V | 23.90 kg |
| KPD-950х950-2-PV230-SN | KPD-950х950-2-PV230-SN | No | Yes | 15 VA | 950 mm | 980 mm | 1010 mm | 490 mm | 960 mm | Steel, galvanized | 950 mm | 980 mm | 1010 mm | 375 mm  [stored 1.23031 ft] | 1010 mm | 960 mm | 1010 mm | 1 | Yes | 230 V | 23.90 kg |
| KPD-950х950-2-PV24-VN | KPD-950х950-2-PV24-VN | Yes | No | 18 VA | 950 mm | 980 mm | 1010 mm | 490 mm | 960 mm | Steel, galvanized | 950 mm | 980 mm | 1010 mm | 375 mm  [stored 1.23031 ft] | 1010 mm | 960 mm | 1010 mm | 1 | Yes | 24 V | 23.90 kg |
| KPD-950х950-2-PV24-SN | KPD-950х950-2-PV24-SN | No | Yes | 18 VA | 950 mm | 980 mm | 1010 mm | 490 mm | 960 mm | Steel, galvanized | 950 mm | 980 mm | 1010 mm | 375 mm  [stored 1.23031 ft] | 1010 mm | 960 mm | 1010 mm | 1 | Yes | 24 V | 23.90 kg |
| KPD-1000х1000-1-PV230-VN | KPD-1000х1000-1-PV230-VN | Yes | No | 15 VA | 1000 mm | 1030 mm | 1060 mm | 515 mm | 1010 mm | Steel, galvanized | 1000 mm | 1030 mm | 1060 mm | 400 mm  [stored 1.31234 ft] | 1060 mm | 1010 mm | 1060 mm | 1 | No | 230 V | 25.60 kg |
| KPD-1000х1000-1-PV230-SN | KPD-1000х1000-1-PV230-SN | No | Yes | 15 VA | 1000 mm | 1030 mm | 1060 mm | 515 mm | 1010 mm | Steel, galvanized | 1000 mm | 1030 mm | 1060 mm | 400 mm  [stored 1.31234 ft] | 1060 mm | 1010 mm | 1060 mm | 1 | No | 230 V | 25.60 kg |
| KPD-1000х1000-1-PV24-VN | KPD-1000х1000-1-PV24-VN | Yes | No | 18 VA | 1000 mm | 1030 mm | 1060 mm | 515 mm | 1010 mm | Steel, galvanized | 1000 mm | 1030 mm | 1060 mm | 400 mm  [stored 1.31234 ft] | 1060 mm | 1010 mm | 1060 mm | 1 | No | 24 V | 25.60 kg |
| KPD-1000х1000-1-PV24-SN | KPD-1000х1000-1-PV24-SN | No | Yes | 18 VA | 1000 mm | 1030 mm | 1060 mm | 515 mm | 1010 mm | Steel, galvanized | 1000 mm | 1030 mm | 1060 mm | 400 mm  [stored 1.31234 ft] | 1060 mm | 1010 mm | 1060 mm | 1 | No | 24 V | 25.60 kg |
| KPD-1000х1000-2-PV230-VN | KPD-1000х1000-2-PV230-VN | Yes | No | 15 VA | 1000 mm | 1030 mm | 1060 mm | 515 mm | 1010 mm | Steel, galvanized | 1000 mm | 1030 mm | 1060 mm | 400 mm  [stored 1.31234 ft] | 1060 mm | 1010 mm | 1060 mm | 1 | Yes | 230 V | 25.60 kg |
| KPD-1000х1000-2-ПВ230-СН | KPD-1000х1000-2-ПВ230-СН | No | Yes | 15 VA | 1000 mm | 1030 mm | 1060 mm | 515 mm | 1010 mm | Steel, galvanized | 1000 mm | 1030 mm | 1060 mm | 400 mm  [stored 1.31234 ft] | 1060 mm | 1010 mm | 1060 mm | 1 | Yes | 230 V | 25.60 kg |
| KPD-1000х1000-2-PV24-VN | KPD-1000х1000-2-PV24-VN | Yes | No | 18 VA | 1000 mm | 1030 mm | 1060 mm | 515 mm | 1010 mm | Steel, galvanized | 1000 mm | 1030 mm | 1060 mm | 400 mm  [stored 1.31234 ft] | 1060 mm | 1010 mm | 1060 mm | 1 | Yes | 24 V | 25.60 kg |
| KPD-1000х1000-2-PV24-SN | KPD-1000х1000-2-ПВ24-СН | No | Yes | 18 VA | 1000 mm | 1030 mm | 1060 mm | 515 mm | 1010 mm | Steel, galvanized | 1000 mm | 1030 mm | 1060 mm | 400 mm  [stored 1.31234 ft] | 1060 mm | 1010 mm | 1060 mm | 1 | Yes | 24 V | 25.60 kg |
| KPD-1050х1050-1-PV230-VN | KPD-1050х1050-1-PV230-VN | Yes | No | 15 VA | 1050 mm | 1080 mm | 1110 mm | 540 mm | 1060 mm | Steel, galvanized | 1050 mm | 1080 mm | 1110 mm | 425 mm  [stored 1.39436 ft] | 1110 mm | 1060 mm | 1110 mm | 2 | No | 230 V | 28.00 kg |
| KPD-1050х1050-1-PV230-SN | KPD-1050х1050-1-PV230-SN | No | Yes | 15 VA | 1050 mm | 1080 mm | 1110 mm | 540 mm | 1060 mm | Steel, galvanized | 1050 mm | 1080 mm | 1110 mm | 425 mm  [stored 1.39436 ft] | 1110 mm | 1060 mm | 1110 mm | 2 | No | 230 V | 28.00 kg |
| KPD-1050х1050-1-PV24-VN | KPD-1050х1050-1-PV24-VN | Yes | No | 18 VA | 1050 mm | 1080 mm | 1110 mm | 540 mm | 1060 mm | Steel, galvanized | 1050 mm | 1080 mm | 1110 mm | 425 mm  [stored 1.39436 ft] | 1110 mm | 1060 mm | 1110 mm | 2 | No | 24 V | 28.00 kg |
| KPD-1050х1050-1-PV24-SN | KPD-1050х1050-1-PV24-SN | No | Yes | 18 VA | 1050 mm | 1080 mm | 1110 mm | 540 mm | 1060 mm | Steel, galvanized | 1050 mm | 1080 mm | 1110 mm | 425 mm  [stored 1.39436 ft] | 1110 mm | 1060 mm | 1110 mm | 2 | No | 24 V | 28.00 kg |
| KPD-1050х1050-2-PV230-VN | KPD-1050х1050-2-PV230-VN | Yes | No | 15 VA | 1050 mm | 1080 mm | 1110 mm | 540 mm | 1060 mm | Steel, galvanized | 1050 mm | 1080 mm | 1110 mm | 425 mm  [stored 1.39436 ft] | 1110 mm | 1060 mm | 1110 mm | 2 | Yes | 230 V | 28.00 kg |
| KPD-1050х1050-2-PV230-SN | KPD-1050х1050-2-PV230-SN | No | Yes | 15 VA | 1050 mm | 1080 mm | 1110 mm | 540 mm | 1060 mm | Steel, galvanized | 1050 mm | 1080 mm | 1110 mm | 425 mm  [stored 1.39436 ft] | 1110 mm | 1060 mm | 1110 mm | 2 | Yes | 230 V | 28.00 kg |
| KPD-1050х1050-2-PV24-VN | KPD-1050х1050-2-PV24-VN | Yes | No | 18 VA | 1050 mm | 1080 mm | 1110 mm | 540 mm | 1060 mm | Steel, galvanized | 1050 mm | 1080 mm | 1110 mm | 425 mm  [stored 1.39436 ft] | 1110 mm | 1060 mm | 1110 mm | 2 | Yes | 24 V | 28.00 kg |
| KPD-1050х1050-2-PV24-SN | KPD-1050х1050-2-PV24-SN | No | Yes | 18 VA | 1050 mm | 1080 mm | 1110 mm | 540 mm | 1060 mm | Steel, galvanized | 1050 mm | 1080 mm | 1110 mm | 425 mm  [stored 1.39436 ft] | 1110 mm | 1060 mm | 1110 mm | 2 | Yes | 24 V | 28.00 kg |
| KPD-1100х1100-1-PV230-VN | KPD-1100х1100-1-PV230-VN | Yes | No | 15 VA | 1100 mm | 1130 mm | 1160 mm | 565 mm | 1110 mm | Steel, galvanized | 1100 mm | 1130 mm | 1160 mm | 450 mm  [stored 1.47638 ft] | 1160 mm | 1110 mm | 1160 mm | 2 | No | 230 V | 30.50 kg |
| KPD-1100х1100-1-PV230-SN | KPD-1100х1100-1-PV230-SN | No | Yes | 15 VA | 1100 mm | 1130 mm | 1160 mm | 565 mm | 1110 mm | Steel, galvanized | 1100 mm | 1130 mm | 1160 mm | 450 mm  [stored 1.47638 ft] | 1160 mm | 1110 mm | 1160 mm | 2 | No | 230 V | 30.50 kg |
| KPD-1100х1100-1-PV24-VN | KPD-1100х1100-1-PV24-VN | Yes | No | 18 VA | 1100 mm | 1130 mm | 1160 mm | 565 mm | 1110 mm | Steel, galvanized | 1100 mm | 1130 mm | 1160 mm | 450 mm  [stored 1.47638 ft] | 1160 mm | 1110 mm | 1160 mm | 2 | No | 24 V | 30.50 kg |
| KPD-1100х1100-1-PV24-SN | KPD-1100х1100-1-PV24-SN | No | Yes | 18 VA | 1100 mm | 1130 mm | 1160 mm | 565 mm | 1110 mm | Steel, galvanized | 1100 mm | 1130 mm | 1160 mm | 450 mm  [stored 1.47638 ft] | 1160 mm | 1110 mm | 1160 mm | 2 | No | 24 V | 30.50 kg |
| KPD-1100х1100-2-PV230-VN | KPD-1100х1100-2-PV230-VN | Yes | No | 15 VA | 1100 mm | 1130 mm | 1160 mm | 565 mm | 1110 mm | Steel, galvanized | 1100 mm | 1130 mm | 1160 mm | 450 mm  [stored 1.47638 ft] | 1160 mm | 1110 mm | 1160 mm | 2 | Yes | 230 V | 30.50 kg |
| KPD-1100х1100-2-PV230-SN | KPD-1100х1100-2-PV230-SN | No | Yes | 15 VA | 1100 mm | 1130 mm | 1160 mm | 565 mm | 1110 mm | Steel, galvanized | 1100 mm | 1130 mm | 1160 mm | 450 mm  [stored 1.47638 ft] | 1160 mm | 1110 mm | 1160 mm | 2 | Yes | 230 V | 30.50 kg |
| KPD-1100х1100-2-PV24-VN | KPD-1100х1100-2-PV24-VN | Yes | No | 18 VA | 1100 mm | 1130 mm | 1160 mm | 565 mm | 1110 mm | Steel, galvanized | 1100 mm | 1130 mm | 1160 mm | 450 mm  [stored 1.47638 ft] | 1160 mm | 1110 mm | 1160 mm | 2 | Yes | 24 V | 30.50 kg |
| KPD-1100х1100-2-PV24-SN | KPD-1100х1100-2-PV24-SN | No | Yes | 18 VA | 1100 mm | 1130 mm | 1160 mm | 565 mm | 1110 mm | Steel, galvanized | 1100 mm | 1130 mm | 1160 mm | 450 mm  [stored 1.47638 ft] | 1160 mm | 1110 mm | 1160 mm | 2 | Yes | 24 V | 30.50 kg |
| KPD-1150х1150-1-PV230-VN | KPD-1150х1150-1-PV230-VN | Yes | No | 15 VA | 1150 mm | 1180 mm | 1210 mm | 590 mm | 1160 mm | Steel, galvanized | 1150 mm | 1180 mm | 1210 mm | 475 mm  [stored 1.5584 ft] | 1210 mm | 1160 mm | 1210 mm | 2 | No | 230 V | 33.00 kg |
| KPD-1150х1150-1-PV230-SN | KPD-1150х1150-1-PV230-SN | No | Yes | 15 VA | 1150 mm | 1180 mm | 1210 mm | 590 mm | 1160 mm | Steel, galvanized | 1150 mm | 1180 mm | 1210 mm | 475 mm  [stored 1.5584 ft] | 1210 mm | 1160 mm | 1210 mm | 2 | No | 230 V | 33.00 kg |
| KPD-1150х1150-1-PV24-VN | KPD-1150х1150-1-PV24-VN | Yes | No | 18 VA | 1150 mm | 1180 mm | 1210 mm | 590 mm | 1160 mm | Steel, galvanized | 1150 mm | 1180 mm | 1210 mm | 475 mm  [stored 1.5584 ft] | 1210 mm | 1160 mm | 1210 mm | 2 | No | 24 V | 33.00 kg |
| KPD-1150х1150-1-PV24-SN | KPD-1150х1150-1-PV24-SN | No | Yes | 18 VA | 1150 mm | 1180 mm | 1210 mm | 590 mm | 1160 mm | Steel, galvanized | 1150 mm | 1180 mm | 1210 mm | 475 mm  [stored 1.5584 ft] | 1210 mm | 1160 mm | 1210 mm | 2 | No | 24 V | 33.00 kg |
| KPD-1150х1150-2-PV230-VN | KPD-1150х1150-2-PV230-VN | Yes | No | 15 VA | 1150 mm | 1180 mm | 1210 mm | 590 mm | 1160 mm | Steel, galvanized | 1150 mm | 1180 mm | 1210 mm | 475 mm  [stored 1.5584 ft] | 1210 mm | 1160 mm | 1210 mm | 2 | Yes | 230 V | 33.00 kg |
| KPD-1150х1150-2-PV230-SN | KPD-1150х1150-2-PV230-SN | No | Yes | 15 VA | 1150 mm | 1180 mm | 1210 mm | 590 mm | 1160 mm | Steel, galvanized | 1150 mm | 1180 mm | 1210 mm | 475 mm  [stored 1.5584 ft] | 1210 mm | 1160 mm | 1210 mm | 2 | Yes | 230 V | 33.00 kg |
| KPD-1150х1150-2-PV24-VN | KPD-1150х1150-2-PV24-VN | Yes | No | 18 VA | 1150 mm | 1180 mm | 1210 mm | 590 mm | 1160 mm | Steel, galvanized | 1150 mm | 1180 mm | 1210 mm | 475 mm  [stored 1.5584 ft] | 1210 mm | 1160 mm | 1210 mm | 2 | Yes | 24 V | 33.00 kg |
| KPD-1150х1150-2-PV24-SN | KPD-1150х1150-2-PV24-SN | No | Yes | 18 VA | 1150 mm | 1180 mm | 1210 mm | 590 mm | 1160 mm | Steel, galvanized | 1150 mm | 1180 mm | 1210 mm | 475 mm  [stored 1.5584 ft] | 1210 mm | 1160 mm | 1210 mm | 2 | Yes | 24 V | 33.00 kg |
| KPD-1200х1200-1-PV230-VN | KPD-1200х1200-1-PV230-VN | Yes | No | 15 VA | 1200 mm | 1230 mm | 1260 mm | 615 mm | 1210 mm | Steel, galvanized | 1200 mm | 1230 mm | 1260 mm | 500 mm | 1260 mm | 1210 mm | 1260 mm | 2 | No | 230 V | 35.50 kg |
| KPD-1200х1200-1-PV230-SN | KPD-1200х1200-1-PV230-SN | No | Yes | 15 VA | 1200 mm | 1230 mm | 1260 mm | 615 mm | 1210 mm | Steel, galvanized | 1200 mm | 1230 mm | 1260 mm | 500 mm | 1260 mm | 1210 mm | 1260 mm | 2 | No | 230 V | 35.50 kg |
| KPD-1200х1200-1-PV24-VN | KPD-1200х1200-1-PV24-VN | Yes | No | 18 VA | 1200 mm | 1230 mm | 1260 mm | 615 mm | 1210 mm | Steel, galvanized | 1200 mm | 1230 mm | 1260 mm | 500 mm | 1260 mm | 1210 mm | 1260 mm | 2 | No | 24 V | 35.50 kg |
| KPD-1200х1200-1-PV24-SN | KPD-1200х1200-1-PV24-SN | No | Yes | 18 VA | 1200 mm | 1230 mm | 1260 mm | 615 mm | 1210 mm | Steel, galvanized | 1200 mm | 1230 mm | 1260 mm | 500 mm | 1260 mm | 1210 mm | 1260 mm | 2 | No | 24 V | 35.50 kg |
| KPD-1200х1200-2-PV230-VN | KPD-1200х1200-2-PV230-VN | Yes | No | 15 VA | 1200 mm | 1230 mm | 1260 mm | 615 mm | 1210 mm | Steel, galvanized | 1200 mm | 1230 mm | 1260 mm | 500 mm | 1260 mm | 1210 mm | 1260 mm | 2 | Yes | 230 V | 35.50 kg |
| KPD-1200х1200-2-PV230-SN | KPD-1200х1200-2-PV230-SN | No | Yes | 15 VA | 1200 mm | 1230 mm | 1260 mm | 615 mm | 1210 mm | Steel, galvanized | 1200 mm | 1230 mm | 1260 mm | 500 mm | 1260 mm | 1210 mm | 1260 mm | 2 | Yes | 230 V | 35.50 kg |
| KPD-1200х1200-2-PV24-VN | KPD-1200х1200-2-PV24-VN | Yes | No | 18 VA | 1200 mm | 1230 mm | 1260 mm | 615 mm | 1210 mm | Steel, galvanized | 1200 mm | 1230 mm | 1260 mm | 500 mm | 1260 mm | 1210 mm | 1260 mm | 2 | Yes | 24 V | 35.50 kg |
| KPD-1200х1200-2-PV24-SN | KPD-1200х1200-2-PV24-SN | No | Yes | 18 VA | 1200 mm | 1230 mm | 1260 mm | 615 mm | 1210 mm | Steel, galvanized | 1200 mm | 1230 mm | 1260 mm | 500 mm | 1260 mm | 1210 mm | 1260 mm | 2 | Yes | 24 V | 35.50 kg |
| KPD-1250х1250-1-PV230-VN | KPD-1250х1250-1-PV230-VN | Yes | No | 15 VA | 1250 mm | 1280 mm | 1310 mm | 640 mm | 1260 mm | Steel, galvanized | 1250 mm | 1280 mm | 1310 mm | 525 mm | 1310 mm | 1260 mm | 1310 mm | 2 | No | 230 V | 38.00 kg |
| KPD-1250х1250-1-PV230-SN | KPD-1250х1250-1-PV230-SN | No | Yes | 15 VA | 1250 mm | 1280 mm | 1310 mm | 640 mm | 1260 mm | Steel, galvanized | 1250 mm | 1280 mm | 1310 mm | 525 mm | 1310 mm | 1260 mm | 1310 mm | 2 | No | 230 V | 38.00 kg |
| KPD-1250х1250-1-PV24-VN | KPD-1250х1250-1-PV24-VN | Yes | No | 18 VA | 1250 mm | 1280 mm | 1310 mm | 640 mm | 1260 mm | Steel, galvanized | 1250 mm | 1280 mm | 1310 mm | 525 mm | 1310 mm | 1260 mm | 1310 mm | 2 | No | 24 V | 38.00 kg |
| KPD-1250х1250-1-PV24-SN | KPD-1250х1250-1-PV24-SN | No | Yes | 18 VA | 1250 mm | 1280 mm | 1310 mm | 640 mm | 1260 mm | Steel, galvanized | 1250 mm | 1280 mm | 1310 mm | 525 mm | 1310 mm | 1260 mm | 1310 mm | 2 | No | 24 V | 38.00 kg |
| KPD-1250х1250-2-PV230-VN | KPD-1250х1250-2-PV230-VN | Yes | No | 15 VA | 1250 mm | 1280 mm | 1310 mm | 640 mm | 1260 mm | Steel, galvanized | 1250 mm | 1280 mm | 1310 mm | 525 mm | 1310 mm | 1260 mm | 1310 mm | 2 | Yes | 230 V | 38.00 kg |
| KPD-1250х1250-2-PV230-SN | KPD-1250х1250-2-PV230-SN | No | Yes | 15 VA | 1250 mm | 1280 mm | 1310 mm | 640 mm | 1260 mm | Steel, galvanized | 1250 mm | 1280 mm | 1310 mm | 525 mm | 1310 mm | 1260 mm | 1310 mm | 2 | Yes | 230 V | 38.00 kg |
| KPD-1250х1250-2-PV24-VN | KPD-1250х1250-2-PV24-VN | Yes | No | 18 VA | 1250 mm | 1280 mm | 1310 mm | 640 mm | 1260 mm | Steel, galvanized | 1250 mm | 1280 mm | 1310 mm | 525 mm | 1310 mm | 1260 mm | 1310 mm | 2 | Yes | 24 V | 38.00 kg |
| KPD-1250х1250-2-PV24-SN | KPD-1250х1250-2-PV24-SN | No | Yes | 18 VA | 1250 mm | 1280 mm | 1310 mm | 640 mm | 1260 mm | Steel, galvanized | 1250 mm | 1280 mm | 1310 mm | 525 mm | 1310 mm | 1260 mm | 1310 mm | 2 | Yes | 24 V | 38.00 kg |
| KPD-1300х1300-1-PV230-VN | KPD-1300х1300-1-PV230-VN | Yes | No | 15 VA | 1300 mm | 1330 mm | 1360 mm | 665 mm | 1310 mm | Steel, galvanized | 1300 mm | 1330 mm | 1360 mm | 550 mm | 1360 mm | 1310 mm | 1360 mm | 4 | No | 230 V | 42.00 kg |
| KPD-1300х1300-1-PV230-SN | KPD-1300х1300-1-PV230-SN | No | Yes | 15 VA | 1300 mm | 1330 mm | 1360 mm | 665 mm | 1310 mm | Steel, galvanized | 1300 mm | 1330 mm | 1360 mm | 550 mm | 1360 mm | 1310 mm | 1360 mm | 4 | No | 230 V | 42.00 kg |
| KPD-1300х1300-1-PV24-VN | KPD-1300х1300-1-PV24-VN | Yes | No | 18 VA | 1300 mm | 1330 mm | 1360 mm | 665 mm | 1310 mm | Steel, galvanized | 1300 mm | 1330 mm | 1360 mm | 550 mm | 1360 mm | 1310 mm | 1360 mm | 4 | No | 24 V | 42.00 kg |
| KPD-1300х1300-1-PV24-SN | KPD-1300х1300-1-PV24-SN | No | Yes | 18 VA | 1300 mm | 1330 mm | 1360 mm | 665 mm | 1310 mm | Steel, galvanized | 1300 mm | 1330 mm | 1360 mm | 550 mm | 1360 mm | 1310 mm | 1360 mm | 4 | No | 24 V | 42.00 kg |
| KPD-1300х1300-2-PV230-VN | KPD-1300х1300-2-PV230-VN | Yes | No | 15 VA | 1300 mm | 1330 mm | 1360 mm | 665 mm | 1310 mm | Steel, galvanized | 1300 mm | 1330 mm | 1360 mm | 550 mm | 1360 mm | 1310 mm | 1360 mm | 4 | Yes | 230 V | 42.00 kg |
| KPD-1300х1300-2-PV230-SN | KPD-1300х1300-2-PV230-SN | No | Yes | 15 VA | 1300 mm | 1330 mm | 1360 mm | 665 mm | 1310 mm | Steel, galvanized | 1300 mm | 1330 mm | 1360 mm | 550 mm | 1360 mm | 1310 mm | 1360 mm | 4 | Yes | 230 V | 42.00 kg |
| KPD-1300х1300-2-PV24-VN | KPD-1300х1300-2-PV24-VN | Yes | No | 18 VA | 1300 mm | 1330 mm | 1360 mm | 665 mm | 1310 mm | Steel, galvanized | 1300 mm | 1330 mm | 1360 mm | 550 mm | 1360 mm | 1310 mm | 1360 mm | 4 | Yes | 24 V | 42.00 kg |
| KPD-1300х1300-2-PV24-SN | KPD-1300х1300-2-PV24-SN | No | Yes | 18 VA | 1300 mm | 1330 mm | 1360 mm | 665 mm | 1310 mm | Steel, galvanized | 1300 mm | 1330 mm | 1360 mm | 550 mm | 1360 mm | 1310 mm | 1360 mm | 4 | Yes | 24 V | 42.00 kg |
| KPD-1350х1350-1-PV230-VN | KPD-1350х1350-1-PV230-VN | Yes | No | 15 VA | 1350 mm | 1380 mm | 1410 mm | 690 mm | 1360 mm | Steel, galvanized | 1350 mm | 1380 mm | 1410 mm | 575 mm | 1410 mm | 1360 mm | 1410 mm | 4 | No | 230 V | 45.00 kg |
| KPD-1350х1350-1-PV230-SN | KPD-1350х1350-1-PV230-SN | No | Yes | 15 VA | 1350 mm | 1380 mm | 1410 mm | 690 mm | 1360 mm | Steel, galvanized | 1350 mm | 1380 mm | 1410 mm | 575 mm | 1410 mm | 1360 mm | 1410 mm | 4 | No | 230 V | 45.00 kg |
| KPD-1350х1350-1-PV24-VN | KPD-1350х1350-1-PV24-VN | Yes | No | 18 VA | 1350 mm | 1380 mm | 1410 mm | 690 mm | 1360 mm | Steel, galvanized | 1350 mm | 1380 mm | 1410 mm | 575 mm | 1410 mm | 1360 mm | 1410 mm | 4 | No | 24 V | 45.00 kg |
| KPD-1350х1350-1-PV24-SN | KPD-1350х1350-1-PV24-SN | No | Yes | 18 VA | 1350 mm | 1380 mm | 1410 mm | 690 mm | 1360 mm | Steel, galvanized | 1350 mm | 1380 mm | 1410 mm | 575 mm | 1410 mm | 1360 mm | 1410 mm | 4 | No | 24 V | 45.00 kg |
| KPD-1350х1350-2-PV230-VN | KPD-1350х1350-2-PV230-VN | Yes | No | 15 VA | 1350 mm | 1380 mm | 1410 mm | 690 mm | 1360 mm | Steel, galvanized | 1350 mm | 1380 mm | 1410 mm | 575 mm | 1410 mm | 1360 mm | 1410 mm | 4 | Yes | 230 V | 45.00 kg |
| KPD-1350х1350-2-PV230-SN | KPD-1350х1350-2-PV230-SN | No | Yes | 15 VA | 1350 mm | 1380 mm | 1410 mm | 690 mm | 1360 mm | Steel, galvanized | 1350 mm | 1380 mm | 1410 mm | 575 mm | 1410 mm | 1360 mm | 1410 mm | 4 | Yes | 230 V | 45.00 kg |
| KPD-1350х1350-2-PV24-VN | KPD-1350х1350-2-PV24-VN | Yes | No | 18 VA | 1350 mm | 1380 mm | 1410 mm | 690 mm | 1360 mm | Steel, galvanized | 1350 mm | 1380 mm | 1410 mm | 575 mm | 1410 mm | 1360 mm | 1410 mm | 4 | Yes | 24 V | 45.00 kg |
| KPD-1350х1350-2-PV24-SN | KPD-1350х1350-2-PV24-SN | No | Yes | 18 VA | 1350 mm | 1380 mm | 1410 mm | 690 mm | 1360 mm | Steel, galvanized | 1350 mm | 1380 mm | 1410 mm | 575 mm | 1410 mm | 1360 mm | 1410 mm | 4 | Yes | 24 V | 45.00 kg |

note: [stored X ft] marks values corroborated as IEEE doubles in the binary element streams (Revit-internal decimal feet)

## geometry (parser evidence)
native form markers: Blend x2
no freeform markers — native parametric forms only
